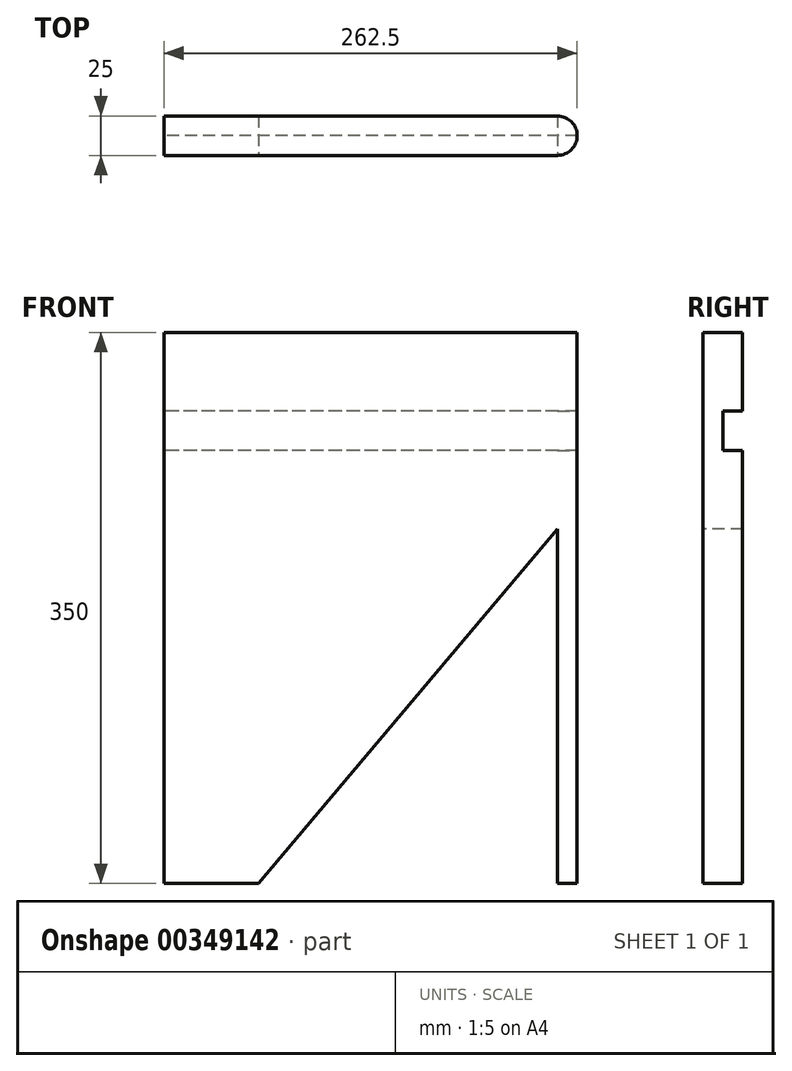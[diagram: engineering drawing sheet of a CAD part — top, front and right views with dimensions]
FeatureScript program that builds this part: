
annotation { "Feature Type Name" : "Feature", "Feature Type Description" : "" }
export const myFeature = defineFeature(function(context is Context, id is Id, definition is map)
    precondition{}
    {
        {
            var Q0;
            Q0=qCreatedBy(makeId("Top.planeOp"),FACE);
            var sketch = newSketch(context, id + "F0", { "sketchPlane" : qUnion([Q0])});
            skLineSegment(sketch, "E0.bottom", {"start": v(0, 0) * mm, "end": v(250, 0) * mm});
            skLineSegment(sketch, "E0.top", {"start": v(0, 25) * mm, "end": v(250, 25) * mm});
            skLineSegment(sketch, "E0.left", {"start": v(0, 0) * mm, "end": v(0, 25) * mm});
            skArc(sketch, "E1", {"start": v(250, 0) * mm, "mid": v(262.5, 12.5) * mm, "end": v(250, 25) * mm});
            skSolve(sketch);
        }
        {
            var Q0;
            Q0=makeQuery(id+"F0.imprint","IMPRINT",FACE,{"disambiguationData":[TD([[makeQuery(id+"F0.imprint","IMPRINT",EDGE,{"derivedFrom":sQuery(id+"F0.wireOp",EDGE,"E0.bottom")}),1.0]])]});
            extrude(context, id + "F1", {"entities" : qUnion([Q0]), "depth" : 350 * mm});
        }
        {
            var Q0;
            Q0=makeQuery(id+"F1.opExtrude","SWEPT_FACE",FACE,{"disambiguationData":[OSD([sQuery(id+"F0.wireOp",EDGE,"E0.left")])]});
            var sketch = newSketch(context, id + "F2", { "sketchPlane" : qUnion([Q0])});
            skLineSegment(sketch, "E2.0", {"start": v(-25, 350) * mm, "end": v(-25, 0) * mm});
            skLineSegment(sketch, "E3.0", {"start": v(0, 350) * mm, "end": v(-25, 350) * mm});
            skLineSegment(sketch, "E4.bottom", {"start": v(-25, 275) * mm, "end": v(-12.5, 275) * mm});
            skLineSegment(sketch, "E4.top", {"start": v(-25, 300) * mm, "end": v(-12.5, 300) * mm});
            skLineSegment(sketch, "E4.left", {"start": v(-25, 300) * mm, "end": v(-25, 275) * mm});
            skLineSegment(sketch, "E4.right", {"start": v(-12.5, 300) * mm, "end": v(-12.5, 275) * mm});
            skLineSegment(sketch, "E5.bottom", {"start": v(-25, 75) * mm, "end": v(-12.5, 75) * mm});
            skLineSegment(sketch, "E5.top", {"start": v(-25, 50) * mm, "end": v(-12.5, 50) * mm});
            skLineSegment(sketch, "E5.left", {"start": v(-25, 75) * mm, "end": v(-25, 50) * mm});
            skLineSegment(sketch, "E5.right", {"start": v(-12.5, 75) * mm, "end": v(-12.5, 50) * mm});
            skSolve(sketch);
        }
        {
            var Q0;
            Q0=makeQuery(id+"F2.imprint","IMPRINT",FACE,{"disambiguationData":[TD([[makeQuery(id+"F2.imprint","IMPRINT",EDGE,{"derivedFrom":sQuery(id+"F2.wireOp",EDGE,"E4.bottom")}),1.0]])]});
            extrude(context, id + "F3", {"entities" : qUnion([Q0]), "operationType" : NewBodyOperationType.REMOVE, "endBound" : BoundingType.THROUGH_ALL, "oppositeDirection" : true, "depth" : 25 * mm});
        }
        {
            var Q0;
            Q0=makeQuery(id+"F1.opExtrude","SWEPT_FACE",FACE,{"disambiguationData":[OSD([sQuery(id+"F0.wireOp",EDGE,"E0.bottom")])]});
            var sketch = newSketch(context, id + "F4", { "sketchPlane" : qUnion([Q0])});
            skLineSegment(sketch, "E6", {"start": v(262.5, 350) * mm, "end": v(262.5, 0) * mm});
            skLineSegment(sketch, "E7", {"start": v(60, 0) * mm, "end": v(262.5, 240) * mm});
            skLineSegment(sketch, "E8", {"start": v(262.5, 240) * mm, "end": v(262.5, 0) * mm});
            skLineSegment(sketch, "E9", {"start": v(60, 0) * mm, "end": v(262.5, 0) * mm});
            skSolve(sketch);
        }
        {
            var Q0;
            {var subQ0=sQuery(id+"F4.wireOp",EDGE,"E9");var subQ1=sQuery(id+"F4.wireOp",EDGE,"E7");var subQ2=sQuery(id+"F0.wireOp",EDGE,"E0.bottom");var subQ3=makeQuery(id+"F4.imprint","INTERSECT",VERTEX,{"derivedFrom":[makeQuery(id+"F1.opExtrude","CAP_EDGE",EDGE,{"disambiguationData":[OSD([subQ2])],"isStart":true}),subQ1,subQ0]});Q0=makeQuery(id+"F4.imprint","IMPRINT",FACE,{"disambiguationData":[TD([[makeQuery(id+"F4.imprint","IMPRINT",EDGE,{"disambiguationData":[TD([[subQ3,-1.0]])],"derivedFrom":subQ1}),-1.0]])]});}
            var Q1;
            {var subQ0=sQuery(id+"F4.wireOp",EDGE,"E8");Q1=makeQuery(id+"F4.imprint","IMPRINT",FACE,{"disambiguationData":[TD([[makeQuery(id+"F4.imprint","IMPRINT",EDGE,{"derivedFrom":subQ0}),-1.0]])]});}
            extrude(context, id + "F5", {"entities" : qUnion([Q0, Q1]), "operationType" : NewBodyOperationType.REMOVE, "endBound" : BoundingType.THROUGH_ALL, "oppositeDirection" : true, "depth" : 25 * mm});
        }
    });
